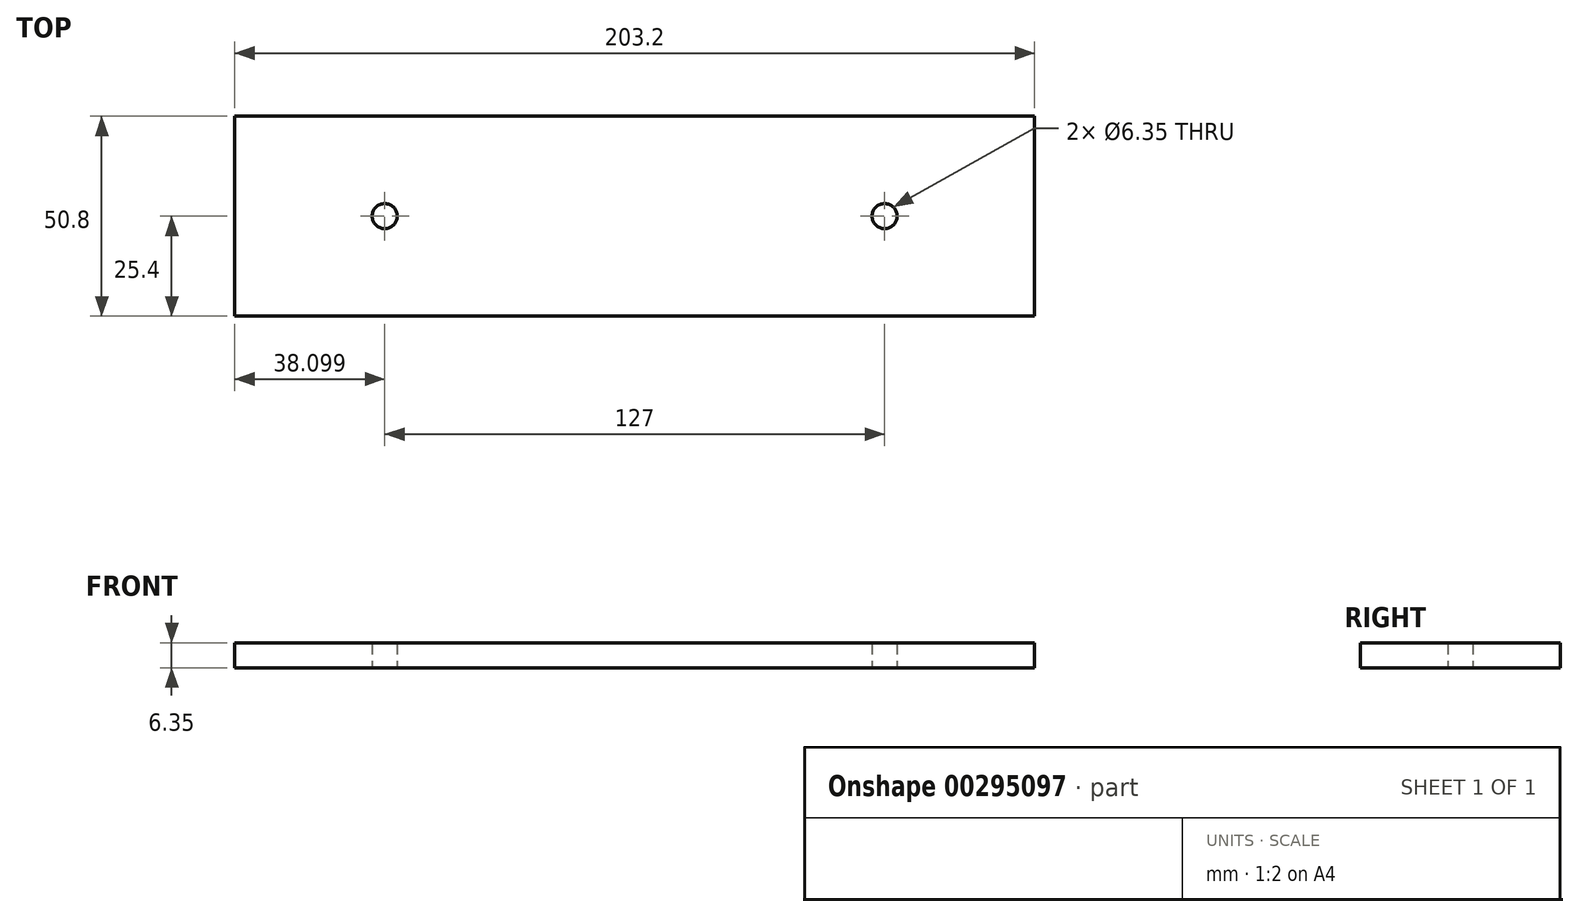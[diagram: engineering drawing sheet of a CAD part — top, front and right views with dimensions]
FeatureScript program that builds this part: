
annotation { "Feature Type Name" : "Feature", "Feature Type Description" : "" }
export const myFeature = defineFeature(function(context is Context, id is Id, definition is map)
    precondition{}
    {
        {
            var Q0;
            Q0=qCreatedBy(makeId("Top.planeOp"),FACE);
            var sketch = newSketch(context, id + "F0", { "sketchPlane" : qUnion([Q0])});
            skLineSegment(sketch, "E0", {"start": v(-109.66, 50.8) * mm, "end": v(93.54, 50.8) * mm});
            skLineSegment(sketch, "E1", {"start": v(93.54, 50.8) * mm, "end": v(93.54, 0) * mm});
            skLineSegment(sketch, "E2", {"start": v(93.54, 0) * mm, "end": v(-109.66, 0) * mm});
            skLineSegment(sketch, "E3", {"start": v(-109.66, 0) * mm, "end": v(-109.66, 50.8) * mm});
            skCircle(sketch, "E4", {"center": v(55.44, 25.4) * mm, "radius": 3.18 * mm});
            skCircle(sketch, "E5", {"center": v(-71.56, 25.4) * mm, "radius": 3.18 * mm});
            skSolve(sketch);
        }
        {
            var Q0;
            Q0=makeQuery(id+"F0.imprint","IMPRINT",FACE,{"disambiguationData":[TD([[makeQuery(id+"F0.imprint","IMPRINT",EDGE,{"derivedFrom":sQuery(id+"F0.wireOp",EDGE,"E0")}),-1.0]])]});
            extrude(context, id + "F1", {"entities" : qUnion([Q0]), "depth" : 6.35 * mm});
        }
    });
